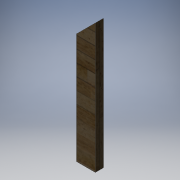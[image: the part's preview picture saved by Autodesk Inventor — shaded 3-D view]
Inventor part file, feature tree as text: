
AUTODESK INVENTOR PART (.ipt)
format: ipt  version: 2016 (Build 200138000, 138)  size: 100,864 bytes
history: native  units: in
note: dims shown in document units (in); Inventor stores cm internally (conversion verified against a paired STEP export)
features: extrude x1, sketch x1
ambient origin geometry x8: Origin, YZ Plane, XZ Plane, XY Plane, X Axis, Y Axis, Z Axis, Center Point
bodies: Solid1 (feature_tree)
feature tree (2):
  extrude  "Extrusion1"  Depth=1.5in
  sketch  "Sketch1"  dims[d1=3.5in d2=24.266in d3=1.5in d4=0.0in d5=45.0deg]
